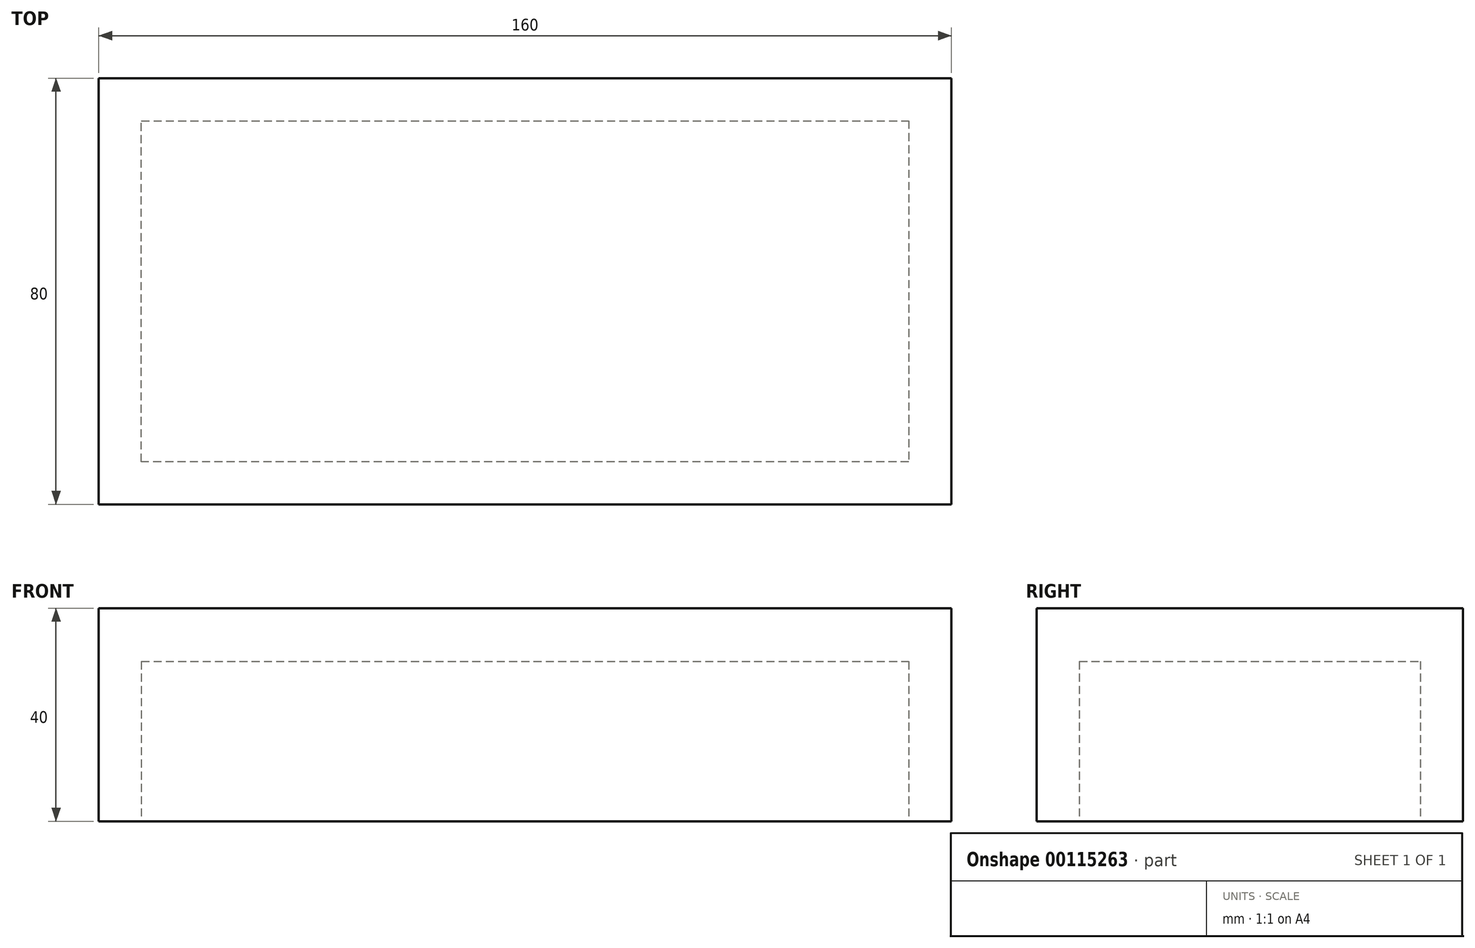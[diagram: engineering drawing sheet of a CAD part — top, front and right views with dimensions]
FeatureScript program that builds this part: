
annotation { "Feature Type Name" : "Feature", "Feature Type Description" : "" }
export const myFeature = defineFeature(function(context is Context, id is Id, definition is map)
    precondition{}
    {
        {
            var Q0;
            Q0=qCreatedBy(makeId("Top.planeOp"),FACE);
            var sketch = newSketch(context, id + "F0", { "sketchPlane" : qUnion([Q0])});
            skLineSegment(sketch, "E0.bottom", {"start": v(-91.73, 19.26) * mm, "end": v(68.27, 19.26) * mm});
            skLineSegment(sketch, "E0.top", {"start": v(-91.73, -60.74) * mm, "end": v(68.27, -60.74) * mm});
            skLineSegment(sketch, "E0.left", {"start": v(-91.73, 19.26) * mm, "end": v(-91.73, -60.74) * mm});
            skLineSegment(sketch, "E0.right", {"start": v(68.27, 19.26) * mm, "end": v(68.27, -60.74) * mm});
            skSolve(sketch);
        }
        {
            var Q0;
            Q0=makeQuery(id+"F0.imprint","IMPRINT",FACE,{"disambiguationData":[TD([[makeQuery(id+"F0.imprint","IMPRINT",EDGE,{"derivedFrom":sQuery(id+"F0.wireOp",EDGE,"E0.bottom")}),-1.0]])]});
            extrude(context, id + "F1", {"entities" : qUnion([Q0]), "depth" : 40 * mm});
        }
        {
            var Q0;
            Q0=qCreatedBy(makeId("Top.planeOp"),FACE);
            var sketch = newSketch(context, id + "F2", { "sketchPlane" : qUnion([Q0])});
            skLineSegment(sketch, "E1.0", {"start": v(-83.73, 11.26) * mm, "end": v(60.27, 11.26) * mm});
            skLineSegment(sketch, "E1.1", {"start": v(-83.73, -52.74) * mm, "end": v(-83.73, 11.26) * mm});
            skLineSegment(sketch, "E1.2", {"start": v(60.27, -52.74) * mm, "end": v(-83.73, -52.74) * mm});
            skLineSegment(sketch, "E1.3", {"start": v(60.27, 11.26) * mm, "end": v(60.27, -52.74) * mm});
            skSolve(sketch);
        }
        {
            var Q0;
            Q0=makeQuery(id+"F2.imprint","IMPRINT",FACE,{"disambiguationData":[TD([[makeQuery(id+"F2.imprint","IMPRINT",EDGE,{"derivedFrom":sQuery(id+"F2.wireOp",EDGE,"E1.0")}),-1.0]])]});
            extrude(context, id + "F3", {"entities" : qUnion([Q0]), "operationType" : NewBodyOperationType.REMOVE, "depth" : 30 * mm});
        }
    });
